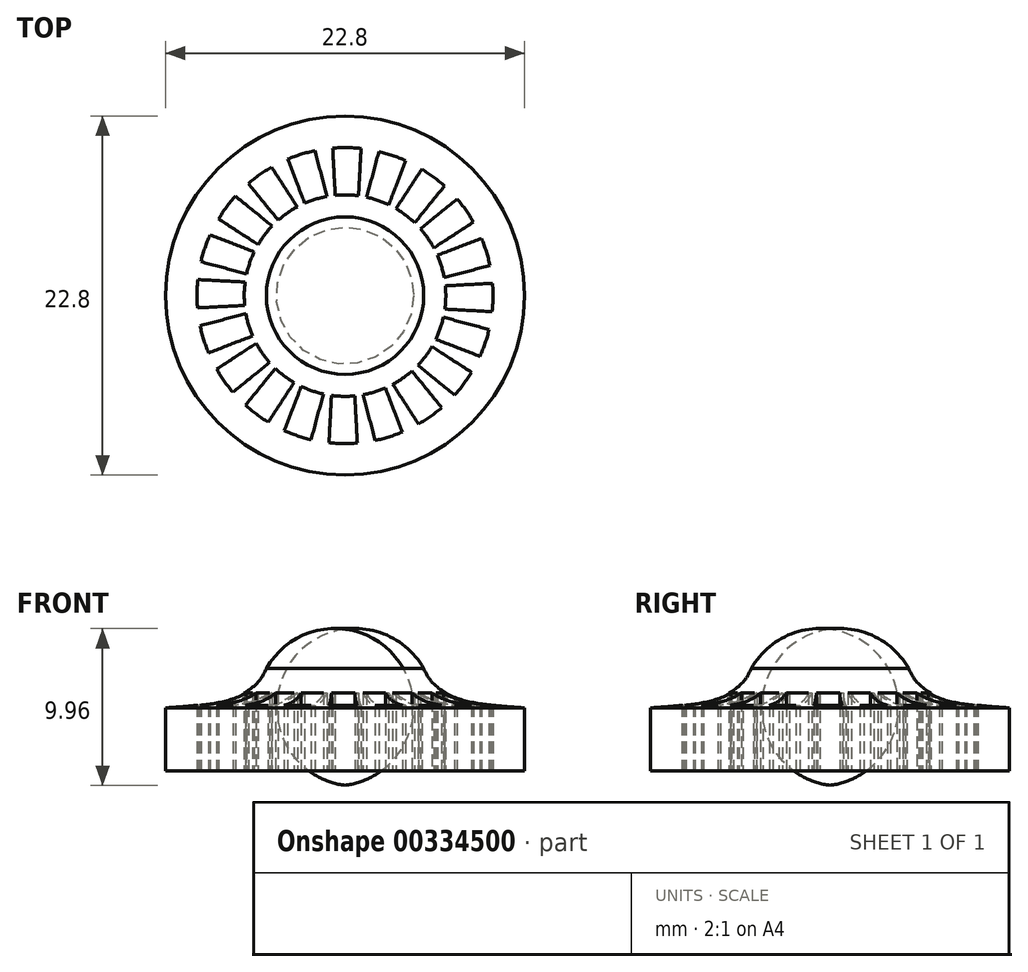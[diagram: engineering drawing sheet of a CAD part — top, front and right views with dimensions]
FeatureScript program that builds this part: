
annotation { "Feature Type Name" : "Feature", "Feature Type Description" : "" }
export const myFeature = defineFeature(function(context is Context, id is Id, definition is map)
    precondition{}
    {
        {
            var Q0;
            Q0=qCreatedBy(makeId("Top.planeOp"),FACE);
            var sketch = newSketch(context, id + "F0", { "sketchPlane" : qUnion([Q0])});
            skCircle(sketch, "E0", {"center": v(0, 0) * mm, "radius": 11.4 * mm});
            skSolve(sketch);
        }
        {
            var Q0;
            Q0=qSketchRegion(id+"F0",true);
            extrude(context, id + "F1", {"entities" : qUnion([Q0]), "depth" : 4 * mm});
        }
        {
            var Q0;
            Q0=qCreatedBy(makeId("Front.planeOp"),FACE);
            var sketch = newSketch(context, id + "F2", { "sketchPlane" : qUnion([Q0])});
            skLineSegment(sketch, "E1.0", {"start": v(-11.4, 4) * mm, "end": v(11.4, 4) * mm});
            skLineSegment(sketch, "E2", {"start": v(0, 4) * mm, "end": v(0, 9) * mm});
            skPoint(sketch, "E2.endSnap0", {"position": v(0, 4) * mm});
            skArc(sketch, "E3", {"start": v(5, 6.5) * mm, "mid": v(2.88, 8.51) * mm, "end": v(0, 9) * mm});
            skFitSpline(sketch, "E4", {"points": [v(5, 6.5) * mm, v(5.45, 5.72) * mm, v(6.64, 4.83) * mm, v(8.6, 4.27) * mm, v(11.4, 4) * mm], "startDerivative": vector(2.01, -4.35) * mm, "endDerivative": vector(9.13, -0.63) * mm});
            skSolve(sketch);
        }
        {
            var Q0;
            Q0=qSketchRegion(id+"F2",true);
            var Q1;
            Q1=sQuery(id+"F2.wireOp",EDGE,"E2");
            revolve(context, id + "F3", {"operationType" : NewBodyOperationType.ADD, "entities" : qUnion([Q0]), "axis" : qUnion([Q1]), "revolveType" : RevolveType.FULL});
        }
        {
            var Q0;
            Q0=makeQuery(id+"F1.opExtrude","CAP_FACE",FACE,{"disambiguationData":[OSD([sQuery(id+"F0.wireOp",EDGE,"E0")])],"isStart":true});
            var sketch = newSketch(context, id + "F4", { "sketchPlane" : qUnion([Q0])});
            skArc(sketch, "E5.0", {"start": v(0.78, 9.37) * mm, "mid": v(-0.12, 9.4) * mm, "end": v(-1.02, 9.34) * mm});
            skArc(sketch, "E6.0", {"start": v(0.62, 6.37) * mm, "mid": v(-0.12, 6.4) * mm, "end": v(-0.86, 6.34) * mm});
            skLineSegment(sketch, "E7.1.0", {"start": v(0.78, 9.37) * mm, "end": v(0.62, 6.37) * mm});
            skLineSegment(sketch, "E8.MirrorCS", {"start": v(-1.02, 9.34) * mm, "end": v(-0.86, 6.34) * mm});
            skArc(sketch, "E9.1.0", {"start": v(-2.15, 9.15) * mm, "mid": v(-3.02, 8.9) * mm, "end": v(-3.86, 8.57) * mm});
            skLineSegment(sketch, "E9.1.1", {"start": v(-2.78, 5.77) * mm, "end": v(-3.86, 8.57) * mm});
            skLineSegment(sketch, "E9.1.2", {"start": v(-1.38, 6.25) * mm, "end": v(-2.15, 9.15) * mm});
            skArc(sketch, "E9.1.3", {"start": v(-1.38, 6.25) * mm, "mid": v(-2.1, 6.05) * mm, "end": v(-2.78, 5.77) * mm});
            skArc(sketch, "E9.2.0", {"start": v(-4.88, 8.04) * mm, "mid": v(-5.62, 7.53) * mm, "end": v(-6.32, 6.96) * mm});
            skLineSegment(sketch, "E9.2.1", {"start": v(-4.42, 4.62) * mm, "end": v(-6.32, 6.96) * mm});
            skLineSegment(sketch, "E9.2.2", {"start": v(-3.24, 5.52) * mm, "end": v(-4.88, 8.04) * mm});
            skArc(sketch, "E9.2.3", {"start": v(-3.24, 5.52) * mm, "mid": v(-3.86, 5.1) * mm, "end": v(-4.42, 4.62) * mm});
            skArc(sketch, "E9.3.0", {"start": v(-7.12, 6.14) * mm, "mid": v(-7.67, 5.43) * mm, "end": v(-8.16, 4.67) * mm});
            skLineSegment(sketch, "E9.3.1", {"start": v(-5.64, 3.03) * mm, "end": v(-8.16, 4.67) * mm});
            skLineSegment(sketch, "E9.3.2", {"start": v(-4.79, 4.25) * mm, "end": v(-7.12, 6.14) * mm});
            skArc(sketch, "E9.3.3", {"start": v(-4.79, 4.25) * mm, "mid": v(-5.25, 3.66) * mm, "end": v(-5.64, 3.03) * mm});
            skArc(sketch, "E9.4.0", {"start": v(-8.67, 3.64) * mm, "mid": v(-8.98, 2.8) * mm, "end": v(-9.2, 1.92) * mm});
            skLineSegment(sketch, "E9.4.1", {"start": v(-6.3, 1.14) * mm, "end": v(-9.2, 1.92) * mm});
            skLineSegment(sketch, "E9.4.2", {"start": v(-5.87, 2.56) * mm, "end": v(-8.67, 3.64) * mm});
            skArc(sketch, "E9.4.3", {"start": v(-5.87, 2.56) * mm, "mid": v(-6.12, 1.86) * mm, "end": v(-6.3, 1.14) * mm});
            skArc(sketch, "E9.5.0", {"start": v(-9.37, 0.78) * mm, "mid": v(-9.4, -0.12) * mm, "end": v(-9.34, -1.02) * mm});
            skLineSegment(sketch, "E9.5.1", {"start": v(-9.34, -1.02) * mm, "end": v(-6.34, -0.86) * mm});
            skLineSegment(sketch, "E9.5.2", {"start": v(-9.37, 0.78) * mm, "end": v(-6.37, 0.62) * mm});
            skArc(sketch, "E9.5.3", {"start": v(-6.37, 0.62) * mm, "mid": v(-6.4, -0.12) * mm, "end": v(-6.34, -0.86) * mm});
            skArc(sketch, "E9.6.0", {"start": v(-9.15, -2.15) * mm, "mid": v(-8.9, -3.02) * mm, "end": v(-8.57, -3.86) * mm});
            skLineSegment(sketch, "E9.6.1", {"start": v(-5.77, -2.78) * mm, "end": v(-8.57, -3.86) * mm});
            skLineSegment(sketch, "E9.6.2", {"start": v(-6.25, -1.38) * mm, "end": v(-9.15, -2.15) * mm});
            skArc(sketch, "E9.6.3", {"start": v(-6.25, -1.38) * mm, "mid": v(-6.05, -2.1) * mm, "end": v(-5.77, -2.78) * mm});
            skArc(sketch, "E9.7.0", {"start": v(-8.04, -4.88) * mm, "mid": v(-7.53, -5.62) * mm, "end": v(-6.96, -6.32) * mm});
            skLineSegment(sketch, "E9.7.1", {"start": v(-4.62, -4.42) * mm, "end": v(-6.96, -6.32) * mm});
            skLineSegment(sketch, "E9.7.2", {"start": v(-5.52, -3.24) * mm, "end": v(-8.04, -4.88) * mm});
            skArc(sketch, "E9.7.3", {"start": v(-5.52, -3.24) * mm, "mid": v(-5.1, -3.86) * mm, "end": v(-4.62, -4.42) * mm});
            skArc(sketch, "E9.8.0", {"start": v(-6.14, -7.12) * mm, "mid": v(-5.43, -7.67) * mm, "end": v(-4.67, -8.16) * mm});
            skLineSegment(sketch, "E9.8.1", {"start": v(-3.03, -5.64) * mm, "end": v(-4.67, -8.16) * mm});
            skLineSegment(sketch, "E9.8.2", {"start": v(-4.25, -4.79) * mm, "end": v(-6.14, -7.12) * mm});
            skArc(sketch, "E9.8.3", {"start": v(-4.25, -4.79) * mm, "mid": v(-3.66, -5.25) * mm, "end": v(-3.03, -5.64) * mm});
            skArc(sketch, "E9.9.0", {"start": v(-3.64, -8.67) * mm, "mid": v(-2.8, -8.98) * mm, "end": v(-1.92, -9.2) * mm});
            skLineSegment(sketch, "E9.9.1", {"start": v(-1.14, -6.3) * mm, "end": v(-1.92, -9.2) * mm});
            skLineSegment(sketch, "E9.9.2", {"start": v(-2.56, -5.87) * mm, "end": v(-3.64, -8.67) * mm});
            skArc(sketch, "E9.9.3", {"start": v(-2.56, -5.87) * mm, "mid": v(-1.86, -6.12) * mm, "end": v(-1.14, -6.3) * mm});
            skArc(sketch, "E9.10.0", {"start": v(-0.78, -9.37) * mm, "mid": v(0.12, -9.4) * mm, "end": v(1.02, -9.34) * mm});
            skLineSegment(sketch, "E9.10.1", {"start": v(1.02, -9.34) * mm, "end": v(0.86, -6.34) * mm});
            skLineSegment(sketch, "E9.10.2", {"start": v(-0.78, -9.37) * mm, "end": v(-0.62, -6.37) * mm});
            skArc(sketch, "E9.10.3", {"start": v(-0.62, -6.37) * mm, "mid": v(0.12, -6.4) * mm, "end": v(0.86, -6.34) * mm});
            skArc(sketch, "E9.11.0", {"start": v(2.15, -9.15) * mm, "mid": v(3.02, -8.9) * mm, "end": v(3.86, -8.57) * mm});
            skLineSegment(sketch, "E9.11.1", {"start": v(2.78, -5.77) * mm, "end": v(3.86, -8.57) * mm});
            skLineSegment(sketch, "E9.11.2", {"start": v(1.38, -6.25) * mm, "end": v(2.15, -9.15) * mm});
            skArc(sketch, "E9.11.3", {"start": v(1.38, -6.25) * mm, "mid": v(2.1, -6.05) * mm, "end": v(2.78, -5.77) * mm});
            skArc(sketch, "E9.12.0", {"start": v(4.88, -8.04) * mm, "mid": v(5.62, -7.53) * mm, "end": v(6.32, -6.96) * mm});
            skLineSegment(sketch, "E9.12.1", {"start": v(4.42, -4.62) * mm, "end": v(6.32, -6.96) * mm});
            skLineSegment(sketch, "E9.12.2", {"start": v(3.24, -5.52) * mm, "end": v(4.88, -8.04) * mm});
            skArc(sketch, "E9.12.3", {"start": v(3.24, -5.52) * mm, "mid": v(3.86, -5.1) * mm, "end": v(4.42, -4.62) * mm});
            skArc(sketch, "E9.13.0", {"start": v(7.12, -6.14) * mm, "mid": v(7.67, -5.43) * mm, "end": v(8.16, -4.67) * mm});
            skLineSegment(sketch, "E9.13.1", {"start": v(5.64, -3.03) * mm, "end": v(8.16, -4.67) * mm});
            skLineSegment(sketch, "E9.13.2", {"start": v(4.79, -4.25) * mm, "end": v(7.12, -6.14) * mm});
            skArc(sketch, "E9.13.3", {"start": v(4.79, -4.25) * mm, "mid": v(5.25, -3.66) * mm, "end": v(5.64, -3.03) * mm});
            skArc(sketch, "E9.14.0", {"start": v(8.67, -3.64) * mm, "mid": v(8.98, -2.8) * mm, "end": v(9.2, -1.92) * mm});
            skLineSegment(sketch, "E9.14.1", {"start": v(6.3, -1.14) * mm, "end": v(9.2, -1.92) * mm});
            skLineSegment(sketch, "E9.14.2", {"start": v(5.87, -2.56) * mm, "end": v(8.67, -3.64) * mm});
            skArc(sketch, "E9.14.3", {"start": v(5.87, -2.56) * mm, "mid": v(6.12, -1.86) * mm, "end": v(6.3, -1.14) * mm});
            skArc(sketch, "E9.15.0", {"start": v(9.37, -0.78) * mm, "mid": v(9.4, 0.12) * mm, "end": v(9.34, 1.02) * mm});
            skLineSegment(sketch, "E9.15.1", {"start": v(9.34, 1.02) * mm, "end": v(6.34, 0.86) * mm});
            skLineSegment(sketch, "E9.15.2", {"start": v(9.37, -0.78) * mm, "end": v(6.37, -0.62) * mm});
            skArc(sketch, "E9.15.3", {"start": v(6.37, -0.62) * mm, "mid": v(6.4, 0.12) * mm, "end": v(6.34, 0.86) * mm});
            skArc(sketch, "E9.16.0", {"start": v(9.15, 2.15) * mm, "mid": v(8.9, 3.02) * mm, "end": v(8.57, 3.86) * mm});
            skLineSegment(sketch, "E9.16.1", {"start": v(5.77, 2.78) * mm, "end": v(8.57, 3.86) * mm});
            skLineSegment(sketch, "E9.16.2", {"start": v(6.25, 1.38) * mm, "end": v(9.15, 2.15) * mm});
            skArc(sketch, "E9.16.3", {"start": v(6.25, 1.38) * mm, "mid": v(6.05, 2.1) * mm, "end": v(5.77, 2.78) * mm});
            skArc(sketch, "E9.17.0", {"start": v(8.04, 4.88) * mm, "mid": v(7.53, 5.62) * mm, "end": v(6.96, 6.32) * mm});
            skLineSegment(sketch, "E9.17.1", {"start": v(4.62, 4.42) * mm, "end": v(6.96, 6.32) * mm});
            skLineSegment(sketch, "E9.17.2", {"start": v(5.52, 3.24) * mm, "end": v(8.04, 4.88) * mm});
            skArc(sketch, "E9.17.3", {"start": v(5.52, 3.24) * mm, "mid": v(5.1, 3.86) * mm, "end": v(4.62, 4.42) * mm});
            skArc(sketch, "E9.18.0", {"start": v(6.14, 7.12) * mm, "mid": v(5.43, 7.67) * mm, "end": v(4.67, 8.16) * mm});
            skLineSegment(sketch, "E9.18.1", {"start": v(3.03, 5.64) * mm, "end": v(4.67, 8.16) * mm});
            skLineSegment(sketch, "E9.18.2", {"start": v(4.25, 4.79) * mm, "end": v(6.14, 7.12) * mm});
            skArc(sketch, "E9.18.3", {"start": v(4.25, 4.79) * mm, "mid": v(3.66, 5.25) * mm, "end": v(3.03, 5.64) * mm});
            skArc(sketch, "E9.19.0", {"start": v(3.64, 8.67) * mm, "mid": v(2.8, 8.98) * mm, "end": v(1.92, 9.2) * mm});
            skLineSegment(sketch, "E9.19.1", {"start": v(1.14, 6.3) * mm, "end": v(1.92, 9.2) * mm});
            skLineSegment(sketch, "E9.19.2", {"start": v(2.56, 5.87) * mm, "end": v(3.64, 8.67) * mm});
            skArc(sketch, "E9.19.3", {"start": v(2.56, 5.87) * mm, "mid": v(1.86, 6.12) * mm, "end": v(1.14, 6.3) * mm});
            skSolve(sketch);
        }
        {
            var Q0;
            Q0=qSketchRegion(id+"F4",true);
            extrude(context, id + "F5", {"entities" : qUnion([Q0]), "operationType" : NewBodyOperationType.REMOVE, "oppositeDirection" : true, "depth" : 25 * mm});
        }
    });
